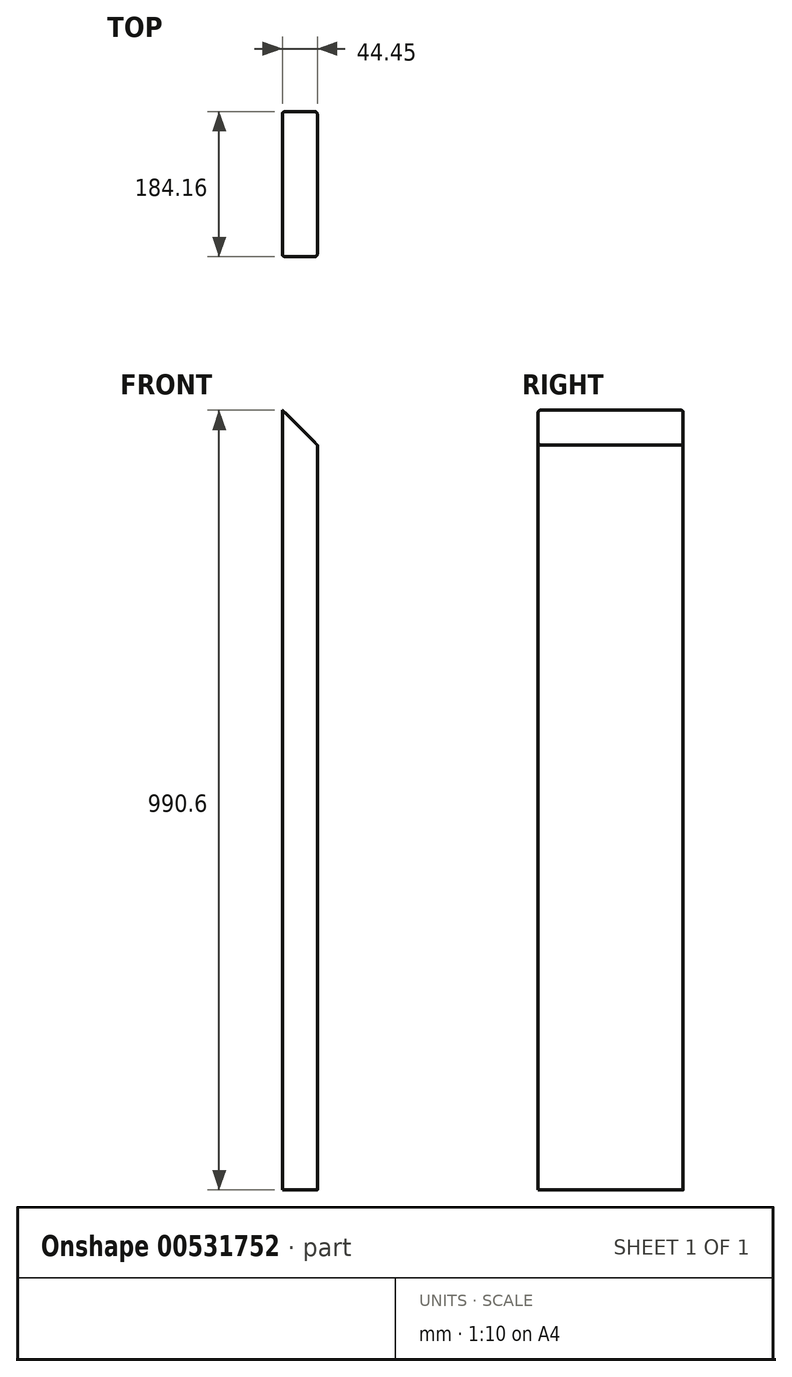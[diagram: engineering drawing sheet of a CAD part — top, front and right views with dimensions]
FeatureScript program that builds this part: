
annotation { "Feature Type Name" : "Feature", "Feature Type Description" : "" }
export const myFeature = defineFeature(function(context is Context, id is Id, definition is map)
    precondition{}
    {
        {
            var Q0;
            Q0=qCreatedBy(makeId("Front.planeOp"),FACE);
            var sketch = newSketch(context, id + "F0", { "sketchPlane" : qUnion([Q0])});
            skLineSegment(sketch, "E0.bottom", {"start": v(0, -208.95) * mm, "end": v(44.45, -208.95) * mm});
            skLineSegment(sketch, "E0.left", {"start": v(0, -208.95) * mm, "end": v(0, 781.65) * mm});
            skLineSegment(sketch, "E0.right", {"start": v(44.45, -208.95) * mm, "end": v(44.45, 737.2) * mm});
            skLineSegment(sketch, "E1", {"start": v(0, 781.65) * mm, "end": v(44.45, 737.2) * mm});
            skSolve(sketch);
        }
        {
            var Q0;
            Q0=makeQuery(id+"F0.imprint","IMPRINT",FACE,{"disambiguationData":[TD([[makeQuery(id+"F0.imprint","IMPRINT",EDGE,{"derivedFrom":sQuery(id+"F0.wireOp",EDGE,"E0.bottom")}),1.0]])]});
            extrude(context, id + "F1", {"entities" : qUnion([Q0]), "endBound" : BoundingType.SYMMETRIC, "depth" : 184.15 * mm, "offsetDistance" : 25.4 * mm});
        }
        {
            var Q0;
            Q0=makeQuery(id+"F1.opExtrude","CAP_EDGE",EDGE,{"disambiguationData":[OSD([sQuery(id+"F0.wireOp",EDGE,"E0.left")])],"isStart":false});
            var Q1;
            Q1=makeQuery(id+"F1.opExtrude","CAP_EDGE",EDGE,{"disambiguationData":[OSD([sQuery(id+"F0.wireOp",EDGE,"E0.right")])],"isStart":false});
            var Q2;
            Q2=makeQuery(id+"F1.opExtrude","CAP_EDGE",EDGE,{"disambiguationData":[OSD([sQuery(id+"F0.wireOp",EDGE,"E0.right")])],"isStart":true});
            var Q3;
            Q3=makeQuery(id+"F1.opExtrude","CAP_EDGE",EDGE,{"disambiguationData":[OSD([sQuery(id+"F0.wireOp",EDGE,"E0.left")])],"isStart":true});
            fillet(context, id + "F2", {"entities" : qUnion([Q0, Q1, Q2, Q3]), "radius" : 3.17 * mm, "tangentPropagation" : true, "allowEdgeOverflow" : false});
        }
    });
